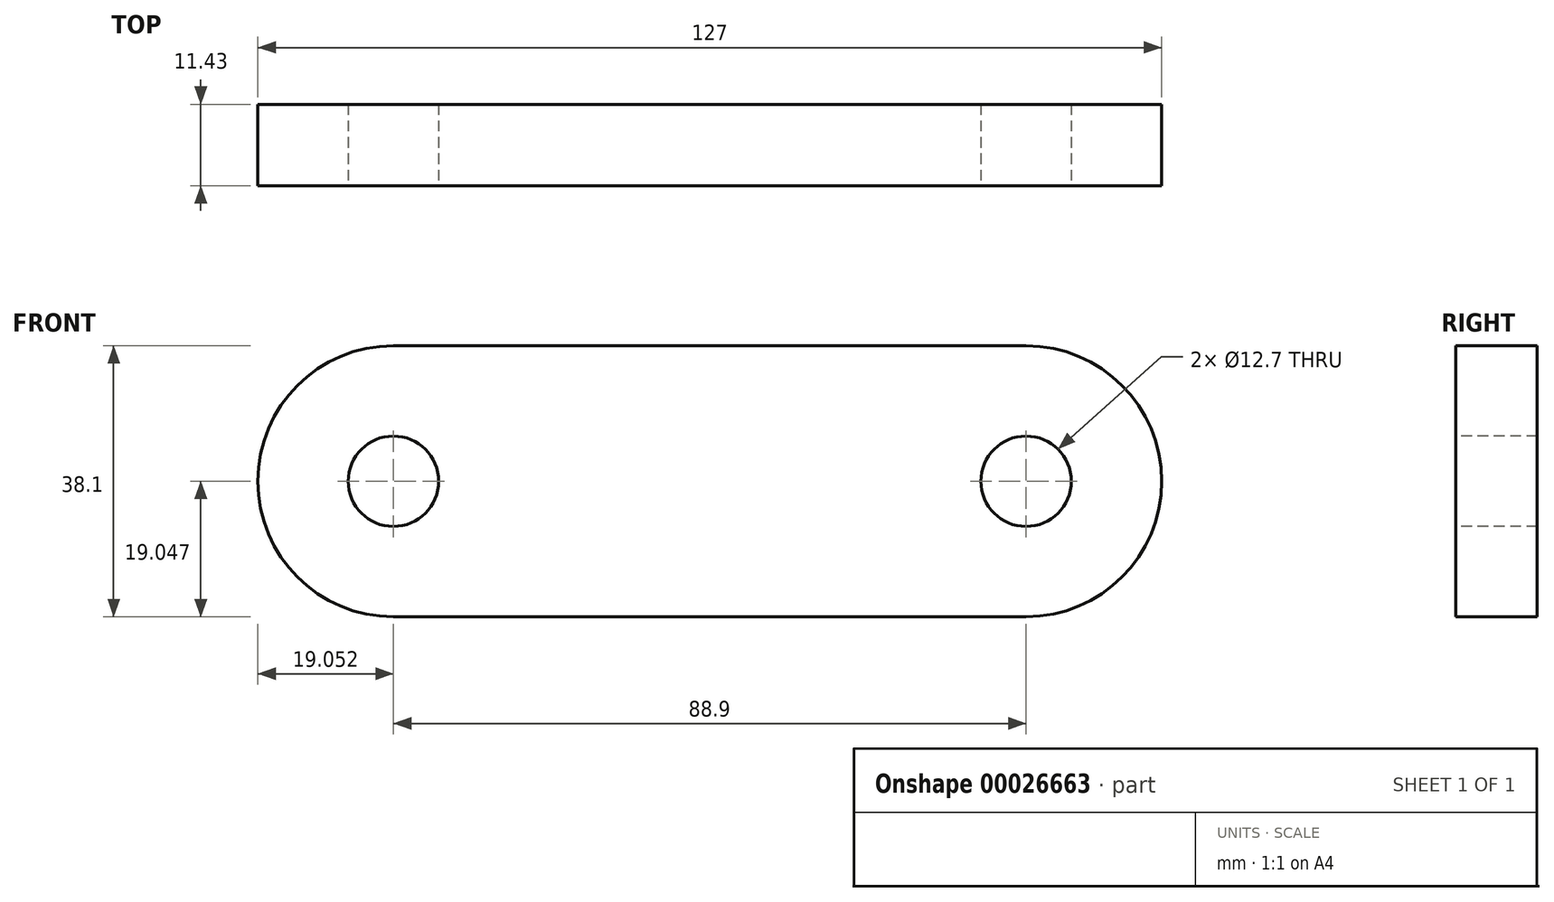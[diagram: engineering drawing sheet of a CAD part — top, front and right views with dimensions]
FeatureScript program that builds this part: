
annotation { "Feature Type Name" : "Feature", "Feature Type Description" : "" }
export const myFeature = defineFeature(function(context is Context, id is Id, definition is map)
    precondition{}
    {
        {
            var Q0;
            Q0=qCreatedBy(makeId("Front.planeOp"),FACE);
            var sketch = newSketch(context, id + "F0", { "sketchPlane" : qUnion([Q0])});
            skLineSegment(sketch, "E0", {"start": v(-89.44, 27.28) * mm, "end": v(-89.44, -10.82) * mm});
            skLineSegment(sketch, "E1", {"start": v(-89.44, -10.82) * mm, "end": v(37.56, -10.82) * mm});
            skLineSegment(sketch, "E2", {"start": v(37.56, -10.82) * mm, "end": v(37.56, 27.28) * mm});
            skLineSegment(sketch, "E3", {"start": v(37.56, 27.28) * mm, "end": v(-89.44, 27.28) * mm});
            skSolve(sketch);
        }
        {
            var Q0;
            Q0=makeQuery(id+"F0.imprint","IMPRINT",FACE,{"disambiguationData":[TD([[makeQuery(id+"F0.imprint","IMPRINT",EDGE,{"derivedFrom":sQuery(id+"F0.wireOp",EDGE,"E0")}),1.0]])]});
            extrude(context, id + "F1", {"entities" : qUnion([Q0]), "depth" : 11.43 * mm});
        }
        {
            var Q0;
            Q0=makeQuery(id+"F1.opExtrude","SWEPT_EDGE",EDGE,{"disambiguationData":[OSD([sQuery(id+"F0.wireOp",EDGE,"E2"),sQuery(id+"F0.wireOp",EDGE,"E3")])]});
            var Q1;
            Q1=makeQuery(id+"F1.opExtrude","SWEPT_EDGE",EDGE,{"disambiguationData":[OSD([sQuery(id+"F0.wireOp",EDGE,"E1"),sQuery(id+"F0.wireOp",EDGE,"E2")])]});
            var Q2;
            Q2=makeQuery(id+"F1.opExtrude","SWEPT_EDGE",EDGE,{"disambiguationData":[OSD([sQuery(id+"F0.wireOp",EDGE,"E0"),sQuery(id+"F0.wireOp",EDGE,"E3")])]});
            var Q3;
            Q3=makeQuery(id+"F1.opExtrude","SWEPT_EDGE",EDGE,{"disambiguationData":[OSD([sQuery(id+"F0.wireOp",EDGE,"E0"),sQuery(id+"F0.wireOp",EDGE,"E1")])]});
            fillet(context, id + "F2", {"entities" : qUnion([Q0, Q1, Q2, Q3]), "radius" : 19.05 * mm, "tangentPropagation" : true, "allowEdgeOverflow" : false});
        }
        {
            var Q0;
            Q0=makeQuery(id+"F1.opExtrude","CAP_FACE",FACE,{"disambiguationData":[OSD([sQuery(id+"F0.wireOp",EDGE,"E0"),sQuery(id+"F0.wireOp",EDGE,"E1"),sQuery(id+"F0.wireOp",EDGE,"E2"),sQuery(id+"F0.wireOp",EDGE,"E3")])],"isStart":false});
            var sketch = newSketch(context, id + "F3", { "sketchPlane" : qUnion([Q0])});
            skCircle(sketch, "E4", {"center": v(-70.39, 8.23) * mm, "radius": 6.35 * mm});
            skCircle(sketch, "E5", {"center": v(18.51, 8.23) * mm, "radius": 6.35 * mm});
            skSolve(sketch);
        }
        {
            var Q0;
            Q0=makeQuery(id+"F3.imprint","IMPRINT",FACE,{"disambiguationData":[TD([[makeQuery(id+"F3.imprint","IMPRINT",EDGE,{"derivedFrom":sQuery(id+"F3.wireOp",EDGE,"E4")}),1.0]])]});
            var Q1;
            Q1=makeQuery(id+"F3.imprint","IMPRINT",FACE,{"disambiguationData":[TD([[makeQuery(id+"F3.imprint","IMPRINT",EDGE,{"derivedFrom":sQuery(id+"F3.wireOp",EDGE,"E5")}),1.0]])]});
            extrude(context, id + "F4", {"entities" : qUnion([Q0, Q1]), "operationType" : NewBodyOperationType.REMOVE, "endBound" : BoundingType.THROUGH_ALL, "oppositeDirection" : true, "depth" : 25.4 * mm});
        }
    });
